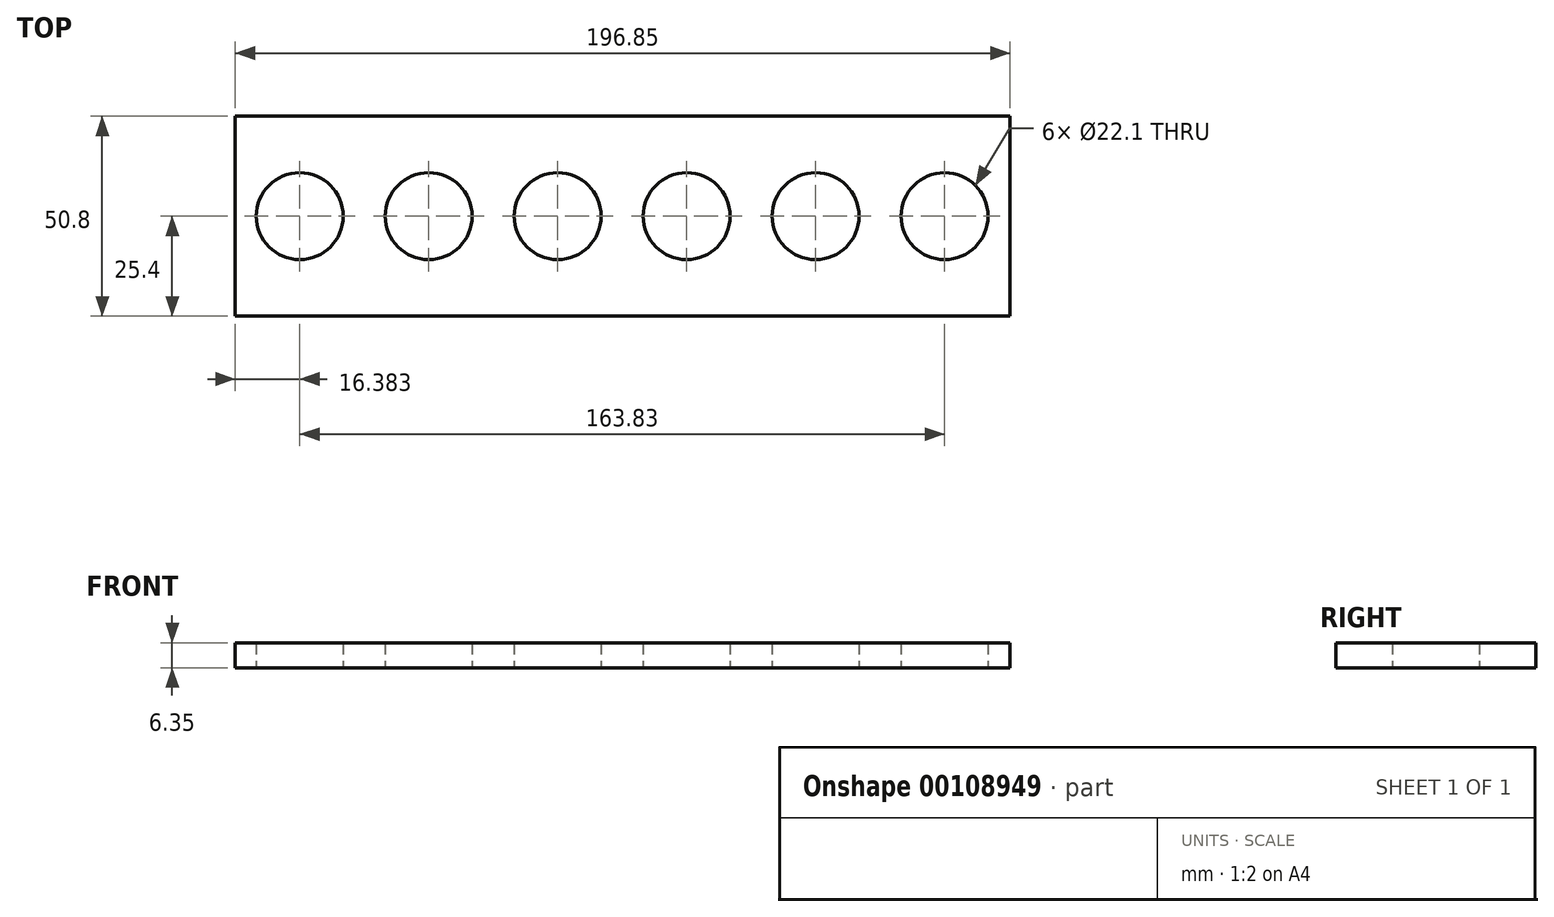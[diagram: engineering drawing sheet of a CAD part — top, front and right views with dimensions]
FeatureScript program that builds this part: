
annotation { "Feature Type Name" : "Feature", "Feature Type Description" : "" }
export const myFeature = defineFeature(function(context is Context, id is Id, definition is map)
    precondition{}
    {
        {
            var Q0;
            Q0=qCreatedBy(makeId("Top.planeOp"),FACE);
            var sketch = newSketch(context, id + "F0", { "sketchPlane" : qUnion([Q0])});
            skLineSegment(sketch, "E0.bottom", {"start": v(0, 0) * mm, "end": v(196.85, 0) * mm});
            skLineSegment(sketch, "E0.top", {"start": v(0, 50.8) * mm, "end": v(196.85, 50.8) * mm});
            skLineSegment(sketch, "E0.left", {"start": v(0, 0) * mm, "end": v(0, 50.8) * mm});
            skLineSegment(sketch, "E0.right", {"start": v(196.85, 0) * mm, "end": v(196.85, 50.8) * mm});
            skCircle(sketch, "E1", {"center": v(16.38, 25.4) * mm, "radius": 11.05 * mm});
            skCircle(sketch, "E2.1.0.0", {"center": v(49.15, 25.4) * mm, "radius": 11.05 * mm});
            skCircle(sketch, "E2.2.0.0", {"center": v(81.92, 25.4) * mm, "radius": 11.05 * mm});
            skCircle(sketch, "E2.3.0.0", {"center": v(114.68, 25.4) * mm, "radius": 11.05 * mm});
            skCircle(sketch, "E2.4.0.0", {"center": v(147.45, 25.4) * mm, "radius": 11.05 * mm});
            skCircle(sketch, "E2.5.0.0", {"center": v(180.21, 25.4) * mm, "radius": 11.05 * mm});
            skLineSegment(sketch, "E2.direction1", {"start": v(16.38, 25.4) * mm, "end": v(49.15, 25.4) * mm, "construction": true});
            skSolve(sketch);
        }
        {
            var Q0;
            Q0=makeQuery(id+"F0.imprint","IMPRINT",FACE,{"disambiguationData":[TD([[makeQuery(id+"F0.imprint","IMPRINT",EDGE,{"derivedFrom":sQuery(id+"F0.wireOp",EDGE,"E0.bottom")}),1.0]])]});
            extrude(context, id + "F1", {"entities" : qUnion([Q0]), "depth" : 6.35 * mm});
        }
    });
